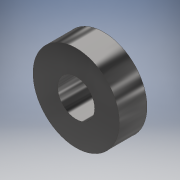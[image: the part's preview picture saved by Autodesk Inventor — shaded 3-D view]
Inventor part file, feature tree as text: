
AUTODESK INVENTOR PART (.ipt)
format: ipt  version: 2018 (Build 220112000, 112)  size: 113,664 bytes
history: native  units: in
note: dims shown in document units (in); Inventor stores cm internally (conversion verified against a paired STEP export)
features: extrude x1, hole x1, sketch x1
ambient origin geometry x8: Origin, YZ Plane, XZ Plane, XY Plane, X Axis, Y Axis, Z Axis, Center Point
bodies: Body1 (feature_tree)
feature tree (3):
  extrude  "Extrusion1"  Depth=0.28in TaperAngle=0.0deg
  hole  "Hole1"  [1 undecoded]
  sketch  "Sketch1"  dims[d1=0.875in d2=0.28in d3=0.0in d4=1.0in d5=1.0in d6=0.375in d7=0.75in d8=0.375in d9=0.25in d10=0.5635in d11=1.0in d12=0.8108in]
note: 1 required parameter value undecoded (feature->parameter linkage not recoverable at this tier; creation-order binding heuristic only, values carry confidence <= 0.55)
